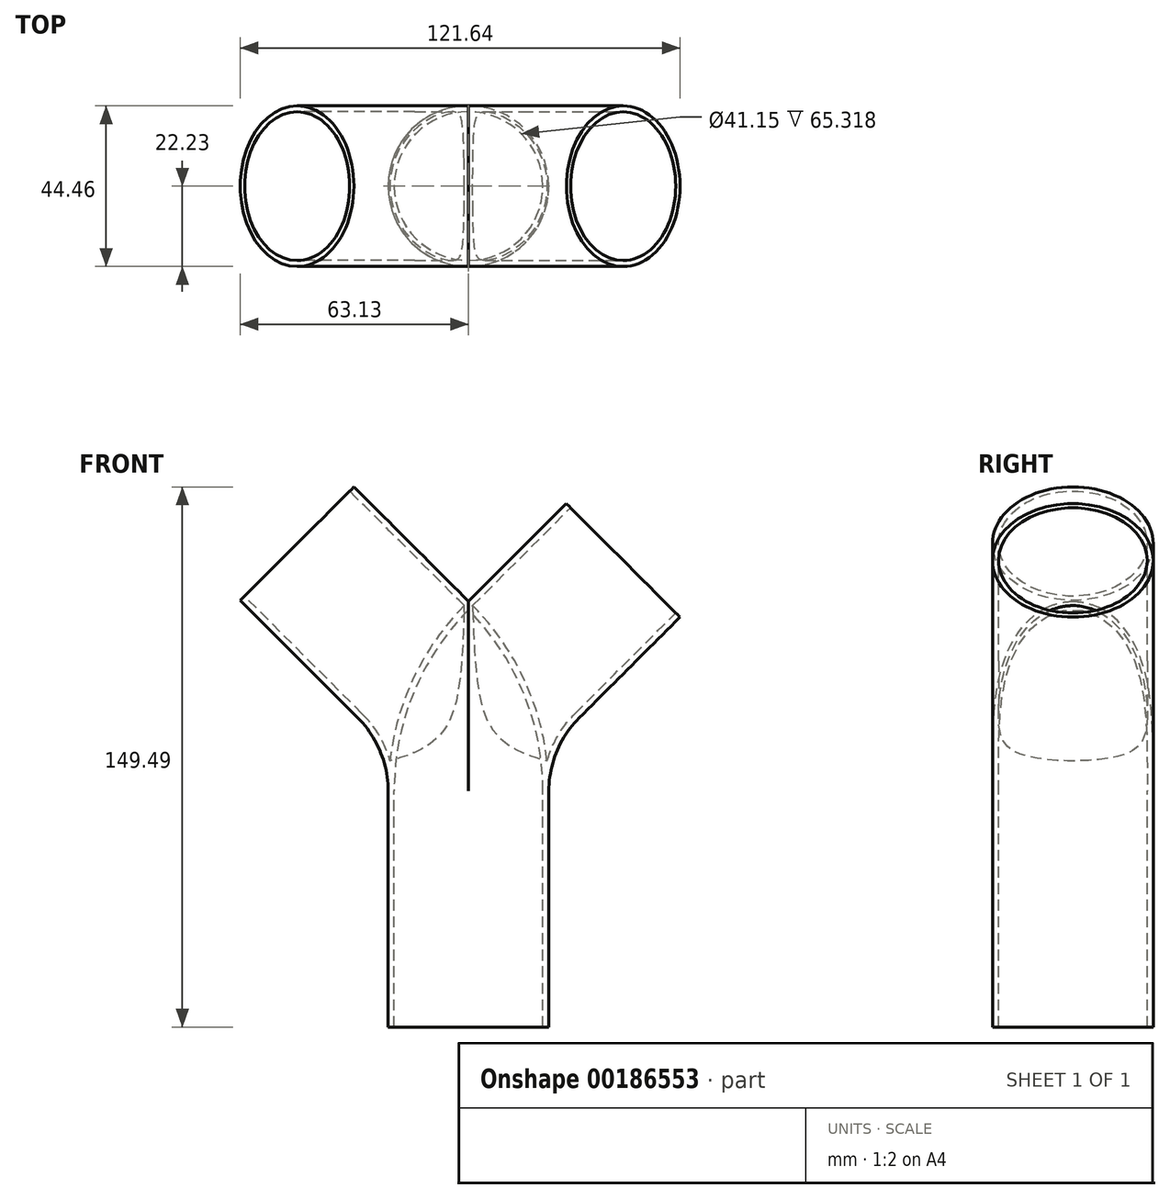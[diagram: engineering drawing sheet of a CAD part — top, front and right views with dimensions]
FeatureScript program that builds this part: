
annotation { "Feature Type Name" : "Feature", "Feature Type Description" : "" }
export const myFeature = defineFeature(function(context is Context, id is Id, definition is map)
    precondition{}
    {
        {
            var Q0;
            Q0=qCreatedBy(makeId("Front.planeOp"),FACE);
            var sketch = newSketch(context, id + "F0", { "sketchPlane" : qUnion([Q0])});
            skLineSegment(sketch, "E0", {"start": v(0, 0) * mm, "end": v(0, 65.32) * mm});
            skLineSegment(sketch, "E1", {"start": v(-14.88, 101.24) * mm, "end": v(-47.42, 133.78) * mm});
            skLineSegment(sketch, "E2", {"start": v(14.88, 101.24) * mm, "end": v(42.79, 129.15) * mm});
            skPoint(sketch, "E3.visualSharp", {"position": v(0, 86.36) * mm});
            skArc(sketch, "E3.filletArc", {"start": v(0, 65.32) * mm, "mid": v(-3.87, 84.76) * mm, "end": v(-14.88, 101.24) * mm});
            skLineSegment(sketch, "E4", {"start": v(0, 65.32) * mm, "end": v(0, 65.32) * mm});
            skArc(sketch, "E5.filletArc", {"start": v(14.88, 101.24) * mm, "mid": v(3.87, 84.76) * mm, "end": v(0, 65.32) * mm});
            skSolve(sketch);
        }
        {
            var Q0;
            Q0=qCreatedBy(makeId("Top.planeOp"),FACE);
            var sketch = newSketch(context, id + "F1", { "sketchPlane" : qUnion([Q0])});
            skCircle(sketch, "E6", {"center": v(0, 0) * mm, "radius": 20.57 * mm});
            skCircle(sketch, "E7", {"center": v(0, 0) * mm, "radius": 22.23 * mm});
            skSolve(sketch);
        }
        {
            var Q0;
            Q0=makeQuery(id+"F1.imprint","IMPRINT",FACE,{"disambiguationData":[TD([[makeQuery(id+"F1.imprint","IMPRINT",EDGE,{"derivedFrom":sQuery(id+"F1.wireOp",EDGE,"E6")}),-1.0]])]});
            var Q1;
            Q1=sQuery(id+"F0.wireOp",EDGE,"E0");
            var Q2;
            Q2=sQuery(id+"F0.wireOp",EDGE,"E3.filletArc");
            var Q3;
            Q3=sQuery(id+"F0.wireOp",EDGE,"E1");
            sweep(context, id + "F2", {"profiles" : qUnion([Q0]), "path" : qUnion([Q1, Q2, Q3])});
        }
        {
            var Q0;
            Q0 = qSketchRegion(id + "F1", true);
            var Q1;
            Q1=sQuery(id+"F0.wireOp",EDGE,"E0");
            var Q2;
            Q2=sQuery(id+"F0.wireOp",EDGE,"E5.filletArc");
            var Q3;
            Q3=sQuery(id+"F0.wireOp",EDGE,"E2");
            sweep(context, id + "F3", {"operationType" : NewBodyOperationType.ADD, "profiles" : qUnion([Q0]), "path" : qUnion([Q1, Q2, Q3])});
        }
    });
